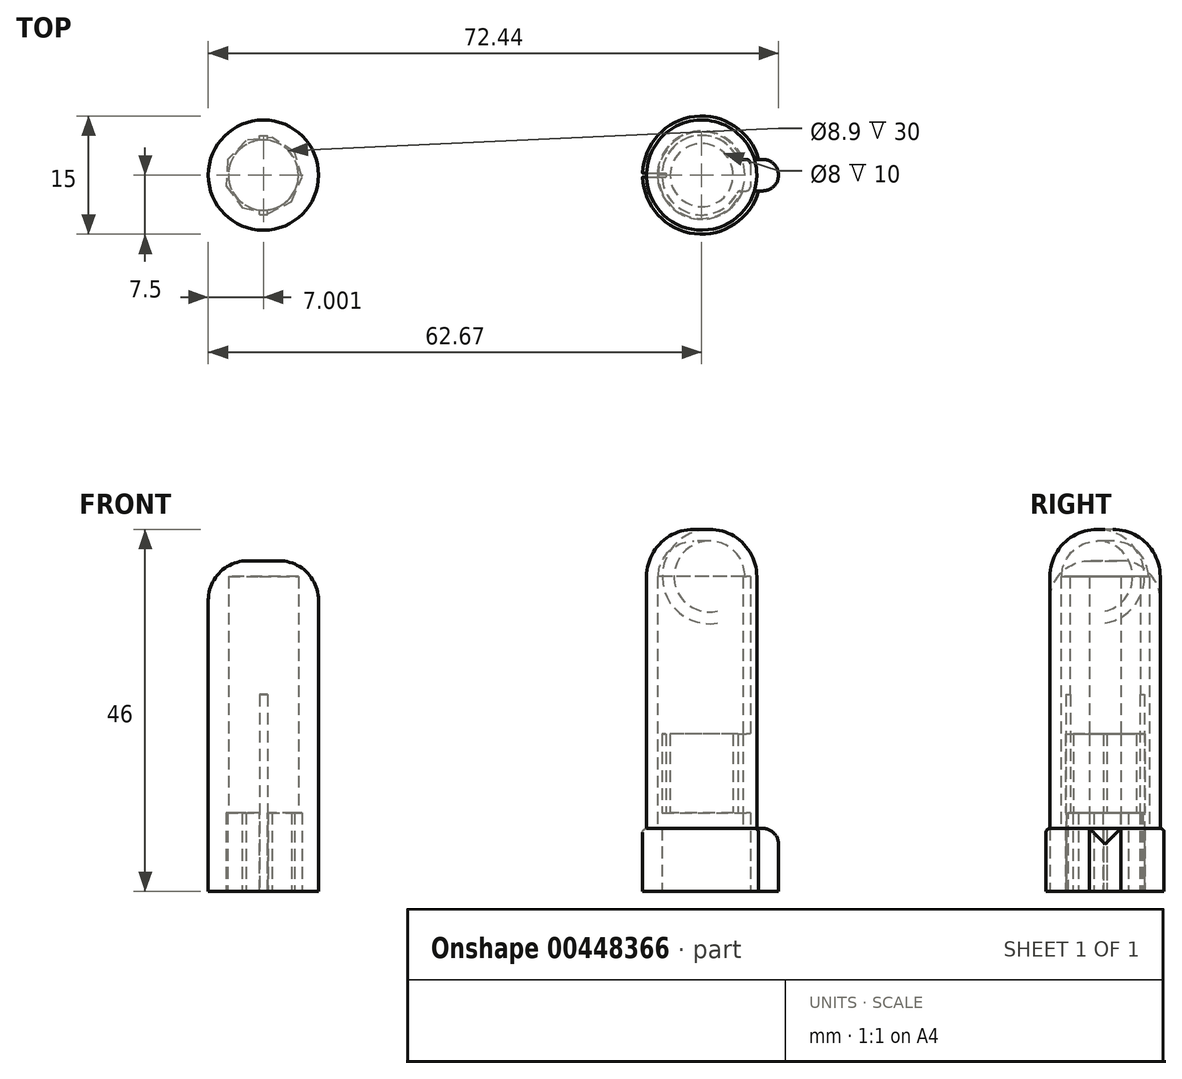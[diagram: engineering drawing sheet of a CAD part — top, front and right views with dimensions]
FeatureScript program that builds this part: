
annotation { "Feature Type Name" : "Feature", "Feature Type Description" : "" }
export const myFeature = defineFeature(function(context is Context, id is Id, definition is map)
    precondition{}
    {
        {
            var Q0;
            Q0=qCreatedBy(makeId("Top.planeOp"),FACE);
            var sketch = newSketch(context, id + "F0", { "sketchPlane" : qUnion([Q0])});
            skArc(sketch, "E0", {"start": v(4.64, 2) * mm, "mid": v(-5.05, 0) * mm, "end": v(4.64, -2) * mm});
            skArc(sketch, "E1", {"start": v(7.23, 2) * mm, "mid": v(-7.5, 0) * mm, "end": v(7.23, -2) * mm});
            skLineSegment(sketch, "E2.bottom", {"start": v(7.23, 2) * mm, "end": v(9.77, 2) * mm});
            skLineSegment(sketch, "E2.top", {"start": v(7.23, -2) * mm, "end": v(9.77, -2) * mm});
            skLineSegment(sketch, "E2.right", {"start": v(9.77, 2) * mm, "end": v(9.77, -2) * mm});
            skLineSegment(sketch, "E3.bottom", {"start": v(4.64, 2) * mm, "end": v(6.17, 2) * mm});
            skLineSegment(sketch, "E3.top", {"start": v(4.64, -2) * mm, "end": v(6.17, -2) * mm});
            skLineSegment(sketch, "E3.right", {"start": v(6.17, 2) * mm, "end": v(6.17, -2) * mm});
            skLineSegment(sketch, "E4.bottom", {"start": v(-9.37, 0.25) * mm, "end": v(-4.54, 0.25) * mm});
            skLineSegment(sketch, "E4.top", {"start": v(-9.37, -0.25) * mm, "end": v(-4.54, -0.25) * mm});
            skLineSegment(sketch, "E4.left", {"start": v(-9.37, 0.25) * mm, "end": v(-9.37, -0.25) * mm});
            skLineSegment(sketch, "E4.right", {"start": v(-4.54, 0.25) * mm, "end": v(-4.54, -0.25) * mm});
            skCircle(sketch, "E5", {"center": v(0, 0) * mm, "radius": 4 * mm});
            skSolve(sketch);
        }
        {
            var Q0;
            Q0=makeQuery(id+"F0.imprint","IMPRINT",FACE,{"disambiguationData":[TD([[makeQuery(id+"F0.imprint","IMPRINT",EDGE,{"derivedFrom":sQuery(id+"F0.wireOp",EDGE,"E0")}),-1.0]])]});
            var Q1;
            {var subQ1=sQuery(id+"F0.wireOp",EDGE,"E2.bottom");Q1=makeQuery(id+"F0.imprint","IMPRINT",FACE,{"disambiguationData":[TD([[makeQuery(id+"F0.imprint","IMPRINT",EDGE,{"derivedFrom":subQ1}),-1.0]])]});}
            var Q2;
            {var subQ0=sQuery(id+"F0.wireOp",EDGE,"E2.left");Q2=makeQuery(id+"F0.imprint","IMPRINT",FACE,{"disambiguationData":[TD([[makeQuery(id+"F0.imprint","IMPRINT",EDGE,{"derivedFrom":subQ0}),1.0]])]});}
            extrude(context, id + "F1", {"entities" : qUnion([Q0, Q1, Q2]), "depth" : 8 * mm});
        }
        {
            var Q0;
            Q0=makeQuery(id+"F1.opExtrude","CAP_FACE",FACE,{"disambiguationData":[OSD([sQuery(id+"F0.wireOp",EDGE,"E0"),sQuery(id+"F0.wireOp",EDGE,"E1")])],"isStart":false});
            var sketch = newSketch(context, id + "F2", { "sketchPlane" : qUnion([Q0])});
            skCircle(sketch, "E6", {"center": v(0, 0) * mm, "radius": 5.6 * mm});
            skCircle(sketch, "E7", {"center": v(0, 0) * mm, "radius": 7 * mm});
            skSolve(sketch);
        }
        {
            var Q0;
            Q0=makeQuery(id+"F2.imprint","IMPRINT",FACE,{"disambiguationData":[TD([[makeQuery(id+"F2.imprint","IMPRINT",EDGE,{"derivedFrom":sQuery(id+"F2.wireOp",EDGE,"E6")}),-1.0]])]});
            var Q1;
            Q1=makeQuery(id+"F2.imprint","IMPRINT",FACE,{"disambiguationData":[TD([[makeQuery(id+"F2.imprint","IMPRINT",EDGE,{"derivedFrom":sQuery(id+"F2.wireOp",EDGE,"E7")}),1.0]])]});
            extrude(context, id + "F3", {"entities" : qUnion([Q0, Q1]), "operationType" : NewBodyOperationType.ADD, "depth" : 32 * mm});
        }
        {
            var Q0;
            Q0=qCreatedBy(makeId("Front.planeOp"),FACE);
            var sketch = newSketch(context, id + "F4", { "sketchPlane" : qUnion([Q0])});
            skLineSegment(sketch, "E8", {"start": v(1, 40) * mm, "end": v(10.08, 40) * mm, "construction": true});
            skLineSegment(sketch, "E9", {"start": v(7, 46.85) * mm, "end": v(7, 34.5) * mm, "construction": true});
            skArc(sketch, "E10", {"start": v(7, 40) * mm, "mid": v(4.87, 44.58) * mm, "end": v(0, 45.92) * mm});
            skArc(sketch, "E11.0", {"start": v(5.5, 40) * mm, "mid": v(3.8, 43.52) * mm, "end": v(0, 44.39) * mm});
            skLineSegment(sketch, "E12", {"start": v(5.5, 40) * mm, "end": v(7, 40) * mm});
            skLineSegment(sketch, "E13", {"start": v(0, 45.92) * mm, "end": v(0, 44.39) * mm});
            skLineSegment(sketch, "E14", {"start": v(0, 50.24) * mm, "end": v(0, 37.13) * mm, "construction": true});
            skSolve(sketch);
        }
        {
            var Q0;
            Q0=makeQuery(id+"F4.imprint","IMPRINT",FACE,{"disambiguationData":[TD([[makeQuery(id+"F4.imprint","IMPRINT",EDGE,{"derivedFrom":sQuery(id+"F4.wireOp",EDGE,"E10")}),1.0]])]});
            var Q1;
            Q1=sQuery(id+"F4.wireOp",EDGE,"E14");
            revolve(context, id + "F5", {"operationType" : NewBodyOperationType.ADD, "entities" : qUnion([Q0]), "axis" : qUnion([Q1]), "revolveType" : RevolveType.FULL});
        }
        {
            var Q0;
            Q0=makeQuery(id+"F1.opExtrude","SWEPT_EDGE",EDGE,{"disambiguationData":[OSD([sQuery(id+"F0.wireOp",EDGE,"E2.top"),sQuery(id+"F0.wireOp",EDGE,"E2.right")])]});
            var Q1;
            Q1=makeQuery(id+"F1.opExtrude","SWEPT_EDGE",EDGE,{"disambiguationData":[OSD([sQuery(id+"F0.wireOp",EDGE,"E2.bottom"),sQuery(id+"F0.wireOp",EDGE,"E2.right")])]});
            var Q2;
            Q2=makeQuery(id+"F1.opExtrude","CAP_EDGE",EDGE,{"disambiguationData":[OSD([sQuery(id+"F0.wireOp",EDGE,"E2.right")])],"isStart":false});
            fillet(context, id + "F6", {"entities" : qUnion([Q0, Q1, Q2]), "radius" : 2 * mm, "tangentPropagation" : true, "allowEdgeOverflow" : false});
        }
        {
            var Q0;
            Q0=makeQuery(id+"F1.opExtrude","CAP_EDGE",EDGE,{"disambiguationData":[OSD([sQuery(id+"F0.wireOp",EDGE,"E1")])],"isStart":false});
            fillet(context, id + "F7", {"entities" : qUnion([Q0]), "radius" : .5 * mm, "tangentPropagation" : true, "allowEdgeOverflow" : false});
        }
        {
            var Q0;
            Q0=makeQuery(id+"F1.opExtrude","SWEPT_EDGE",EDGE,{"disambiguationData":[OSD([sQuery(id+"F0.wireOp",EDGE,"E3.top"),sQuery(id+"F0.wireOp",EDGE,"E3.right")])]});
            var Q1;
            Q1=makeQuery(id+"F1.opExtrude","SWEPT_EDGE",EDGE,{"disambiguationData":[OSD([sQuery(id+"F0.wireOp",EDGE,"E0"),sQuery(id+"F0.wireOp",EDGE,"E3.top")])]});
            var Q2;
            Q2=makeQuery(id+"F1.opExtrude","SWEPT_EDGE",EDGE,{"disambiguationData":[OSD([sQuery(id+"F0.wireOp",EDGE,"E3.bottom"),sQuery(id+"F0.wireOp",EDGE,"E3.right")])]});
            var Q3;
            Q3=makeQuery(id+"F1.opExtrude","SWEPT_EDGE",EDGE,{"disambiguationData":[OSD([sQuery(id+"F0.wireOp",EDGE,"E0"),sQuery(id+"F0.wireOp",EDGE,"E3.bottom")])]});
            fillet(context, id + "F8", {"entities" : qUnion([Q0, Q1, Q2, Q3]), "radius" : .5 * mm, "tangentPropagation" : true, "allowEdgeOverflow" : false});
        }
        {
            var Q0;
            Q0=qCreatedBy(makeId("Top.planeOp"),FACE);
            var sketch = newSketch(context, id + "F9", { "sketchPlane" : qUnion([Q0])});
            skCircle(sketch, "E15", {"center": v(-55.67, 0) * mm, "radius": 4.45 * mm});
            skCircle(sketch, "E16", {"center": v(-55.67, 0) * mm, "radius": 7 * mm});
            skSolve(sketch);
        }
        {
            var Q0;
            Q0=makeQuery(id+"F9.imprint","IMPRINT",FACE,{"disambiguationData":[TD([[makeQuery(id+"F9.imprint","IMPRINT",EDGE,{"derivedFrom":sQuery(id+"F9.wireOp",EDGE,"E15")}),-1.0]])]});
            extrude(context, id + "F10", {"entities" : qUnion([Q0]), "depth" : 40 * mm, "offsetDistance" : 25 * mm});
        }
        {
            var Q0;
            Q0=makeQuery(id+"F10.opExtrude","CAP_FACE",FACE,{"disambiguationData":[OSD([sQuery(id+"F9.wireOp",EDGE,"E15"),sQuery(id+"F9.wireOp",EDGE,"E16")])],"isStart":true});
            var sketch = newSketch(context, id + "F11", { "sketchPlane" : qUnion([Q0])});
            skPoint(sketch, "E17.0.midPoint", {"position": v(-52.33, -2.94) * mm});
            skLineSegment(sketch, "E18.bottom", {"start": v(-65.03, -0.5) * mm, "end": v(-60.19, -0.5) * mm});
            skLineSegment(sketch, "E18.top", {"start": v(-65.03, 0.5) * mm, "end": v(-60.1, 0.5) * mm});
            skLineSegment(sketch, "E18.left", {"start": v(-65.03, -0.5) * mm, "end": v(-65.03, 0.5) * mm});
            skLineSegment(sketch, "E18.right", {"start": v(-47.03, -0.5) * mm, "end": v(-47.03, 0.5) * mm});
            skLineSegment(sketch, "E19.trimOffspring", {"start": v(-51.25, -0.5) * mm, "end": v(-47.03, -0.5) * mm});
            skLineSegment(sketch, "E20.trimOffspring", {"start": v(-51.15, 0.5) * mm, "end": v(-47.03, 0.5) * mm});
            skCircle(sketch, "E21.cCircle", {"center": v(-55.67, 0) * mm, "radius": 4.62 * mm, "construction": true});
            skLineSegment(sketch, "E21.0", {"start": v(-51.73, -2.95) * mm, "end": v(-54.54, -4.8) * mm});
            skLineSegment(sketch, "E21.1", {"start": v(-54.54, -4.8) * mm, "end": v(-57.89, -4.4) * mm});
            skLineSegment(sketch, "E21.2", {"start": v(-57.89, -4.4) * mm, "end": v(-60.2, -1.94) * mm});
            skLineSegment(sketch, "E21.3", {"start": v(-60.2, -1.94) * mm, "end": v(-60.38, 1.42) * mm});
            skLineSegment(sketch, "E21.4", {"start": v(-60.38, 1.42) * mm, "end": v(-58.37, 4.12) * mm});
            skLineSegment(sketch, "E21.5", {"start": v(-58.37, 4.12) * mm, "end": v(-55.09, 4.89) * mm});
            skLineSegment(sketch, "E21.6", {"start": v(-55.09, 4.89) * mm, "end": v(-52.08, 3.37) * mm});
            skLineSegment(sketch, "E21.7", {"start": v(-52.08, 3.37) * mm, "end": v(-50.76, 0.28) * mm});
            skLineSegment(sketch, "E21.8", {"start": v(-50.76, 0.28) * mm, "end": v(-51.73, -2.95) * mm});
            skPoint(sketch, "E21.0.midPoint", {"position": v(-53.14, -3.87) * mm});
            skSolve(sketch);
        }
        {
            var Q0;
            {var subQ0=sQuery(id+"F11.wireOp",EDGE,"E17.6");var subQ1=sQuery(id+"F11.wireOp",EDGE,"E17.5");var subQ2=makeQuery(id+"F11.imprint","INTERSECT",VERTEX,{"derivedFrom":[subQ1,subQ0]});Q0=makeQuery(id+"F11.imprint","IMPRINT",FACE,{"disambiguationData":[TD([[makeQuery(id+"F11.imprint","IMPRINT",EDGE,{"disambiguationData":[TD([[subQ2,1.0]])],"derivedFrom":subQ1}),-1.0]])]});}
            var Q1;
            {var subQ0=sQuery(id+"F11.wireOp",EDGE,"E17.7");var subQ1=sQuery(id+"F11.wireOp",EDGE,"E17.6");var subQ2=makeQuery(id+"F11.imprint","INTERSECT",VERTEX,{"derivedFrom":[subQ1,subQ0]});Q1=makeQuery(id+"F11.imprint","IMPRINT",FACE,{"disambiguationData":[TD([[makeQuery(id+"F11.imprint","IMPRINT",EDGE,{"disambiguationData":[TD([[subQ2,1.0]])],"derivedFrom":subQ1}),-1.0]])]});}
            var Q2;
            {var subQ0=sQuery(id+"F11.wireOp",EDGE,"E17.8");var subQ1=sQuery(id+"F11.wireOp",EDGE,"E17.7");var subQ2=makeQuery(id+"F11.imprint","INTERSECT",VERTEX,{"derivedFrom":[subQ1,subQ0]});Q2=makeQuery(id+"F11.imprint","IMPRINT",FACE,{"disambiguationData":[TD([[makeQuery(id+"F11.imprint","IMPRINT",EDGE,{"disambiguationData":[TD([[subQ2,1.0]])],"derivedFrom":subQ1}),-1.0]])]});}
            var Q3;
            {var subQ0=sQuery(id+"F11.wireOp",EDGE,"E17.9");var subQ1=sQuery(id+"F11.wireOp",EDGE,"E17.0");var subQ2=makeQuery(id+"F11.imprint","INTERSECT",VERTEX,{"derivedFrom":[subQ1,subQ0]});Q3=makeQuery(id+"F11.imprint","IMPRINT",FACE,{"disambiguationData":[TD([[makeQuery(id+"F11.imprint","IMPRINT",EDGE,{"disambiguationData":[TD([[subQ2,-1.0]])],"derivedFrom":subQ1}),-1.0]])]});}
            var Q4;
            {var subQ0=sQuery(id+"F11.wireOp",EDGE,"E17.1");var subQ1=sQuery(id+"F11.wireOp",EDGE,"E17.0");var subQ2=makeQuery(id+"F11.imprint","INTERSECT",VERTEX,{"derivedFrom":[subQ1,subQ0]});Q4=makeQuery(id+"F11.imprint","IMPRINT",FACE,{"disambiguationData":[TD([[makeQuery(id+"F11.imprint","IMPRINT",EDGE,{"disambiguationData":[TD([[subQ2,1.0]])],"derivedFrom":subQ1}),-1.0]])]});}
            var Q5;
            {var subQ0=sQuery(id+"F11.wireOp",EDGE,"E17.2");var subQ1=sQuery(id+"F11.wireOp",EDGE,"E17.1");var subQ2=makeQuery(id+"F11.imprint","INTERSECT",VERTEX,{"derivedFrom":[subQ1,subQ0]});Q5=makeQuery(id+"F11.imprint","IMPRINT",FACE,{"disambiguationData":[TD([[makeQuery(id+"F11.imprint","IMPRINT",EDGE,{"disambiguationData":[TD([[subQ2,1.0]])],"derivedFrom":subQ1}),-1.0]])]});}
            var Q6;
            {var subQ0=sQuery(id+"F11.wireOp",EDGE,"E17.3");var subQ1=sQuery(id+"F11.wireOp",EDGE,"E17.2");var subQ2=makeQuery(id+"F11.imprint","INTERSECT",VERTEX,{"derivedFrom":[subQ1,subQ0]});Q6=makeQuery(id+"F11.imprint","IMPRINT",FACE,{"disambiguationData":[TD([[makeQuery(id+"F11.imprint","IMPRINT",EDGE,{"disambiguationData":[TD([[subQ2,1.0]])],"derivedFrom":subQ1}),-1.0]])]});}
            var Q7;
            {var subQ0=sQuery(id+"F11.wireOp",EDGE,"E17.4");var subQ1=sQuery(id+"F11.wireOp",EDGE,"E17.3");var subQ2=makeQuery(id+"F11.imprint","INTERSECT",VERTEX,{"derivedFrom":[subQ1,subQ0]});Q7=makeQuery(id+"F11.imprint","IMPRINT",FACE,{"disambiguationData":[TD([[makeQuery(id+"F11.imprint","IMPRINT",EDGE,{"disambiguationData":[TD([[subQ2,1.0]])],"derivedFrom":subQ1}),-1.0]])]});}
            var Q8;
            {var subQ0=sQuery(id+"F11.wireOp",EDGE,"E17.5");var subQ1=sQuery(id+"F11.wireOp",EDGE,"E17.4");var subQ2=makeQuery(id+"F11.imprint","INTERSECT",VERTEX,{"derivedFrom":[subQ1,subQ0]});Q8=makeQuery(id+"F11.imprint","IMPRINT",FACE,{"disambiguationData":[TD([[makeQuery(id+"F11.imprint","IMPRINT",EDGE,{"disambiguationData":[TD([[subQ2,1.0]])],"derivedFrom":subQ1}),-1.0]])]});}
            var Q9;
            {var subQ0=sQuery(id+"F11.wireOp",EDGE,"E17.9");var subQ1=sQuery(id+"F11.wireOp",EDGE,"E17.8");var subQ2=makeQuery(id+"F11.imprint","INTERSECT",VERTEX,{"derivedFrom":[subQ1,subQ0]});Q9=makeQuery(id+"F11.imprint","IMPRINT",FACE,{"disambiguationData":[TD([[makeQuery(id+"F11.imprint","IMPRINT",EDGE,{"disambiguationData":[TD([[subQ2,1.0]])],"derivedFrom":subQ1}),-1.0]])]});}
            var Q10;
            {var subQ7=sQuery(id+"F11.wireOp",EDGE,"E21.0");Q10=makeQuery(id+"F11.imprint","IMPRINT",FACE,{"disambiguationData":[TD([[makeQuery(id+"F11.imprint","IMPRINT",EDGE,{"derivedFrom":subQ7}),-1.0]])]});}
            extrude(context, id + "F12", {"entities" : qUnion([Q0, Q1, Q2, Q3, Q4, Q5, Q6, Q7, Q8, Q9, Q10]), "operationType" : NewBodyOperationType.REMOVE, "oppositeDirection" : true, "depth" : 10 * mm, "offsetDistance" : 25 * mm});
        }
        {
            var Q0;
            Q0=makeQuery(id+"F10.opExtrude","CAP_FACE",FACE,{"disambiguationData":[OSD([sQuery(id+"F9.wireOp",EDGE,"E15"),sQuery(id+"F9.wireOp",EDGE,"E16")])],"isStart":false});
            var sketch = newSketch(context, id + "F13", { "sketchPlane" : qUnion([Q0])});
            skCircle(sketch, "E22", {"center": v(-55.67, 0) * mm, "radius": 7 * mm});
            skSolve(sketch);
        }
        {
            var Q0;
            Q0=makeQuery(id+"F13.imprint","IMPRINT",FACE,{"disambiguationData":[TD([[makeQuery(id+"F13.imprint","IMPRINT",EDGE,{"derivedFrom":sQuery(id+"F13.wireOp",EDGE,"E22")}),1.0]])]});
            var Q1;
            Q1=makeQuery(id+"F13.imprint","IMPRINT",FACE,{"disambiguationData":[TD([[makeQuery(id+"F13.imprint","IMPRINT",EDGE,{"derivedFrom":makeQuery(id+"F10.opExtrude","CAP_EDGE",EDGE,{"disambiguationData":[OSD([sQuery(id+"F9.wireOp",EDGE,"E15")])],"isStart":false})}),1.0]])]});
            extrude(context, id + "F14", {"entities" : qUnion([Q0, Q1]), "operationType" : NewBodyOperationType.ADD, "depth" : 2 * mm, "offsetDistance" : 25 * mm});
        }
        {
            var Q0;
            Q0=makeQuery(id+"F14.opExtrude","CAP_EDGE",EDGE,{"disambiguationData":[OSD([sQuery(id+"F13.wireOp",EDGE,"E22")])],"isStart":false});
            fillet(context, id + "F15", {"entities" : qUnion([Q0]), "radius" : 5 * mm, "tangentPropagation" : true, "allowEdgeOverflow" : false});
        }
        {
            var Q0;
            Q0=makeQuery(id+"F10.opExtrude","CAP_FACE",FACE,{"disambiguationData":[OSD([sQuery(id+"F9.wireOp",EDGE,"E15"),sQuery(id+"F9.wireOp",EDGE,"E16")])],"isStart":true});
            var sketch = newSketch(context, id + "F16", { "sketchPlane" : qUnion([Q0])});
            skLineSegment(sketch, "E23.bottom", {"start": v(-56.17, 5) * mm, "end": v(-55.17, 5) * mm});
            skLineSegment(sketch, "E23.top", {"start": v(-56.17, -5) * mm, "end": v(-55.17, -5) * mm});
            skLineSegment(sketch, "E23.left", {"start": v(-56.17, 5) * mm, "end": v(-56.17, -5) * mm});
            skLineSegment(sketch, "E23.right", {"start": v(-55.17, 5) * mm, "end": v(-55.17, -5) * mm});
            skLineSegment(sketch, "E24", {"start": v(-55.67, 0) * mm, "end": v(-55.67, -0.51) * mm, "construction": true});
            skLineSegment(sketch, "E25", {"start": v(-55.67, -0.51) * mm, "end": v(-55.67, 0.63) * mm, "construction": true});
            skSolve(sketch);
        }
        {
            var Q0;
            {var subQ11=sQuery(id+"F16.wireOp",EDGE,"E23.bottom");Q0=makeQuery(id+"F16.imprint","IMPRINT",FACE,{"disambiguationData":[TD([[makeQuery(id+"F16.imprint","IMPRINT",EDGE,{"derivedFrom":subQ11}),-1.0]])]});}
            var Q1;
            {var subQ9=sQuery(id+"F16.wireOp",EDGE,"E23.left");var subQ13=sQuery(id+"F11.wireOp",EDGE,"E17.7");var subQ15=sQuery(id+"F11.wireOp",EDGE,"E17.6");var subQ16=makeQuery(id+"F11.imprint","INTERSECT",VERTEX,{"derivedFrom":[subQ15,subQ13]});var subQ20=makeQuery(id+"F12.boolean.opBoolean","TWEAK_EDGE",EDGE,{"derivedFrom":[makeQuery(id+"F12.opExtrude","CAP_EDGE",EDGE,{"disambiguationData":[OSD([subQ15]),TDD([makeQuery(id+"F11.imprint","IMPRINT",EDGE,{"disambiguationData":[TD([[makeQuery(id+"F11.imprint","INTERSECT",VERTEX,{"derivedFrom":[sQuery(id+"F11.wireOp",EDGE,"E17.5"),subQ15]}),-1.0]])],"derivedFrom":subQ15})])],"isStart":true}),makeQuery(id+"F12.opExtrude","CAP_EDGE",EDGE,{"disambiguationData":[OSD([subQ15]),TDD([makeQuery(id+"F11.imprint","IMPRINT",EDGE,{"disambiguationData":[TD([[subQ16,1.0]])],"derivedFrom":subQ15})])],"isStart":true})]});var subQ21=makeQuery(id+"F16.imprint","INTERSECT",VERTEX,{"derivedFrom":[subQ20,subQ9]});Q1=makeQuery(id+"F16.imprint","IMPRINT",FACE,{"disambiguationData":[TD([[makeQuery(id+"F16.imprint","IMPRINT",EDGE,{"disambiguationData":[TD([[subQ21,-1.0]])],"derivedFrom":subQ9}),1.0]])]});}
            var Q2;
            {var subQ1=sQuery(id+"F16.wireOp",EDGE,"E23.top");Q2=makeQuery(id+"F16.imprint","IMPRINT",FACE,{"disambiguationData":[TD([[makeQuery(id+"F16.imprint","IMPRINT",EDGE,{"derivedFrom":subQ1}),1.0]])]});}
            extrude(context, id + "F17", {"entities" : qUnion([Q0, Q1, Q2]), "operationType" : NewBodyOperationType.REMOVE, "oppositeDirection" : true, "depth" : 25 * mm, "offsetDistance" : 25 * mm});
        }
        {
            var Q0;
            {var subQ0=sQuery(id+"F0.wireOp",EDGE,"E3.bottom");Q0=makeQuery(id+"F0.imprint","IMPRINT",FACE,{"disambiguationData":[TD([[makeQuery(id+"F0.imprint","IMPRINT",EDGE,{"derivedFrom":subQ0}),-1.0]])]});}
            extrude(context, id + "F18", {"entities" : qUnion([Q0]), "operationType" : NewBodyOperationType.ADD, "depth" : 20 * mm, "offsetDistance" : 25 * mm, "hasSecondDirection" : true, "secondDirectionOppositeDirection" : false, "secondDirectionDepth" : 10 * mm});
        }
    });
